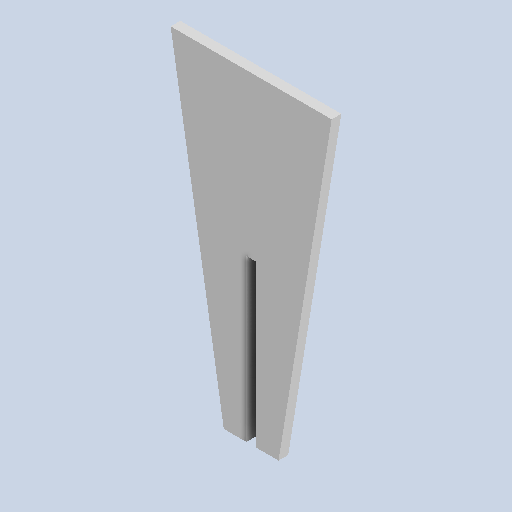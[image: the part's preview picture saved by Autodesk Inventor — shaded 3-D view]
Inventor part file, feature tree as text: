
AUTODESK INVENTOR PART (.ipt)
format: ipt  version: 2022 (Build 260153000, 153)  size: 108,544 bytes
history: native  units: mm
features: other x3, extrude x1, sketch x1, reference x1
ambient origin geometry x8: Origin, YZ Plane, XZ Plane, XY Plane, X Axis, Y Axis, Z Axis, Center Point
bodies: Solid1 (feature_tree)
feature tree (6):
  extrude  "Extrusion1"  Depth=3.0mm
  sketch  "Sketch1"  dims[d0=25.0mm d6=8.5mm d7=17.343229mm d8=50.0mm d9=1.5mm d10=50.0mm d11=3.0mm d12=0.0mm]
  reference  "Reference1"
  other  "<userpath>\OneDrive\Escritorio\Mini_Proyecto_Diseno\Diseno_18012\Modelo_MPD\Carril.iam"
  other  "Carril.iam"
  other  "Pivote_Estructura:1"
